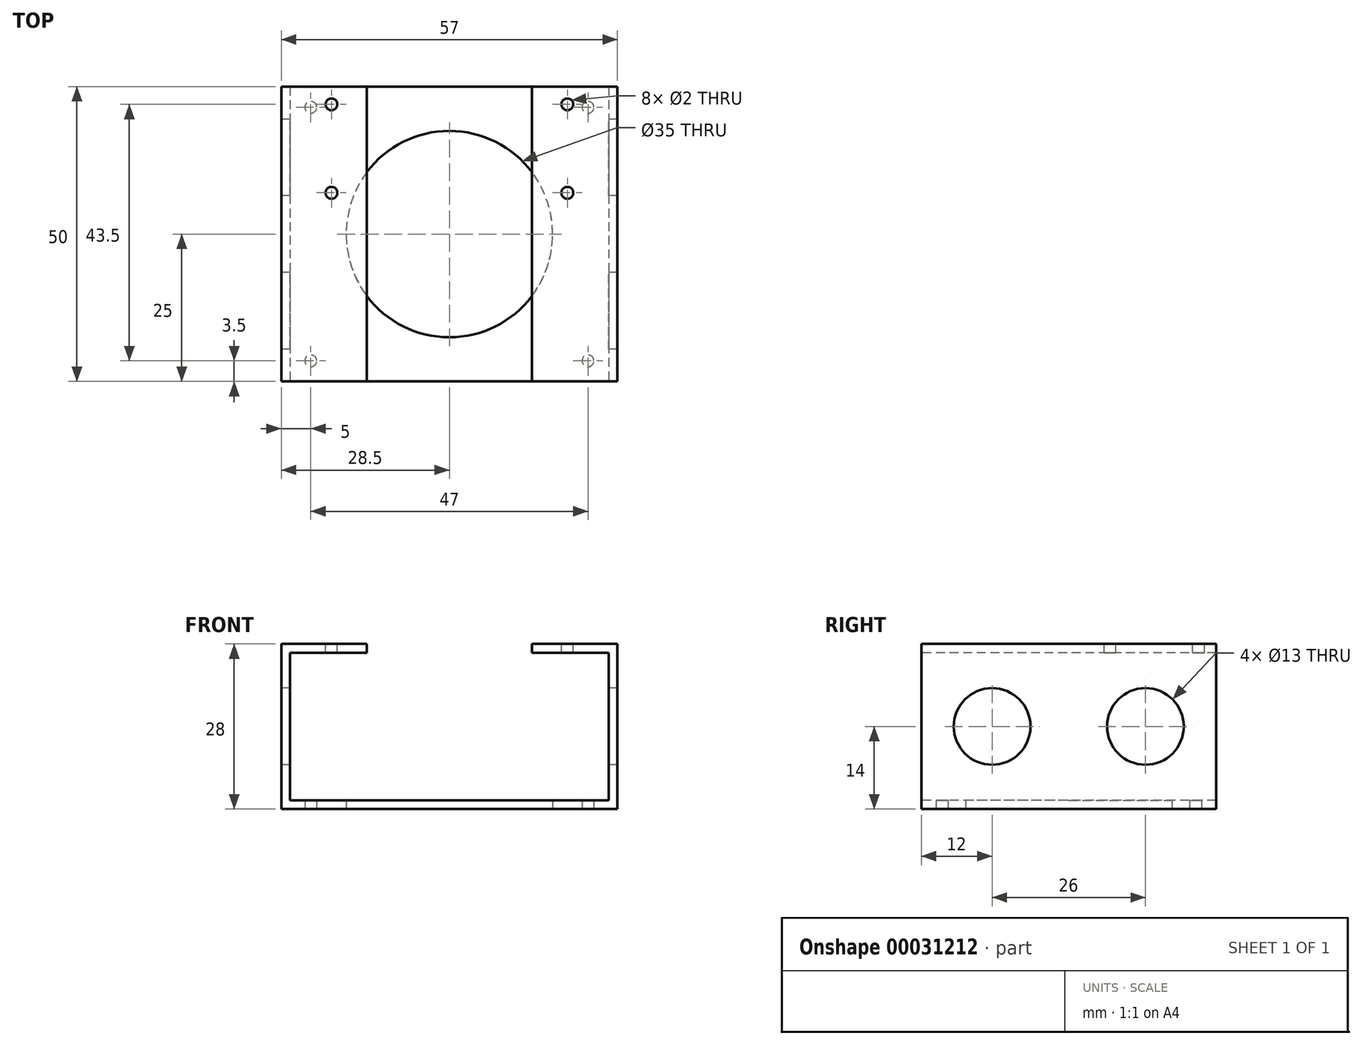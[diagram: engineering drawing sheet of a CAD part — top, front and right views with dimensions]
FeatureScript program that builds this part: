
annotation { "Feature Type Name" : "Feature", "Feature Type Description" : "" }
export const myFeature = defineFeature(function(context is Context, id is Id, definition is map)
    precondition{}
    {
        {
            var Q0;
            Q0=qCreatedBy(makeId("Top.planeOp"),FACE);
            var sketch = newSketch(context, id + "F0", { "sketchPlane" : qUnion([Q0])});
            skLineSegment(sketch, "E0.bottom", {"start": v(-27, 25) * mm, "end": v(27, 25) * mm});
            skLineSegment(sketch, "E0.top", {"start": v(-27, -25) * mm, "end": v(27, -25) * mm});
            skLineSegment(sketch, "E0.left", {"start": v(-27, 25) * mm, "end": v(-27, -25) * mm});
            skLineSegment(sketch, "E0.right", {"start": v(27, 25) * mm, "end": v(27, -25) * mm});
            skPoint(sketch, "E0.middle", {"position": v(0, 0) * mm});
            skLineSegment(sketch, "E1.bottom", {"start": v(-23.5, 21.5) * mm, "end": v(23.5, 21.5) * mm, "construction": true});
            skLineSegment(sketch, "E1.top", {"start": v(-23.5, -21.5) * mm, "end": v(23.5, -21.5) * mm, "construction": true});
            skLineSegment(sketch, "E1.left", {"start": v(-23.5, 21.5) * mm, "end": v(-23.5, -21.5) * mm, "construction": true});
            skLineSegment(sketch, "E1.right", {"start": v(23.5, 21.5) * mm, "end": v(23.5, -21.5) * mm, "construction": true});
            skCircle(sketch, "E2", {"center": v(-23.5, 21.5) * mm, "radius": 1 * mm});
            skCircle(sketch, "E3.MirrorC", {"center": v(23.5, 21.5) * mm, "radius": 1 * mm});
            skCircle(sketch, "E4.MirrorC", {"center": v(-23.5, -21.5) * mm, "radius": 1 * mm});
            skCircle(sketch, "E5.MirrorC", {"center": v(23.5, -21.5) * mm, "radius": 1 * mm});
            skSolve(sketch);
        }
        {
            var Q0;
            Q0 = qSketchRegion(id + "F0", true);
            extrude(context, id + "F1", {"entities" : qUnion([Q0]), "depth" : 1.5 * mm});
        }
        {
            var Q0;
            Q0=qCreatedBy(makeId("Top.planeOp"),FACE);
            var sketch = newSketch(context, id + "F2", { "sketchPlane" : qUnion([Q0])});
            skLineSegment(sketch, "E6.0", {"start": v(27, 25) * mm, "end": v(27, -25) * mm, "construction": true});
            skLineSegment(sketch, "E7.bottom", {"start": v(27, 25) * mm, "end": v(28.5, 25) * mm});
            skLineSegment(sketch, "E7.top", {"start": v(27, -25) * mm, "end": v(28.5, -25) * mm});
            skLineSegment(sketch, "E7.left", {"start": v(27, 25) * mm, "end": v(27, -25) * mm});
            skLineSegment(sketch, "E7.right", {"start": v(28.5, 25) * mm, "end": v(28.5, -25) * mm});
            skSolve(sketch);
        }
        {
            var Q0;
            Q0 = qSketchRegion(id + "F2", true);
            extrude(context, id + "F3", {"entities" : qUnion([Q0]), "operationType" : NewBodyOperationType.ADD, "depth" : (25 + 1.5 + 1.5) * mm});
        }
        {
            var Q0;
            Q0=makeQuery(id+"F3.opExtrude","SWEPT_FACE",FACE,{"disambiguationData":[OSD([sQuery(id+"F2.wireOp",EDGE,"E7.left")])]});
            var sketch = newSketch(context, id + "F4", { "sketchPlane" : qUnion([Q0])});
            skLineSegment(sketch, "E8.bottom", {"start": v(-25, 28) * mm, "end": v(25, 28) * mm});
            skLineSegment(sketch, "E8.top", {"start": v(-25, 26.5) * mm, "end": v(25, 26.5) * mm});
            skLineSegment(sketch, "E8.left", {"start": v(-25, 28) * mm, "end": v(-25, 26.5) * mm});
            skLineSegment(sketch, "E8.right", {"start": v(25, 28) * mm, "end": v(25, 26.5) * mm});
            skSolve(sketch);
        }
        {
            var Q0;
            Q0 = qSketchRegion(id + "F4", true);
            extrude(context, id + "F5", {"entities" : qUnion([Q0]), "operationType" : NewBodyOperationType.ADD, "depth" : 13 * mm});
        }
        {
            var Q0;
            Q0=makeQuery(id+"F5.boolean.opBoolean","MERGE",FACE,{"derivedFrom":[makeQuery(id+"F3.opExtrude","CAP_FACE",FACE,{"disambiguationData":[OSD([sQuery(id+"F2.wireOp",EDGE,"E7.bottom"),sQuery(id+"F2.wireOp",EDGE,"E7.top"),sQuery(id+"F2.wireOp",EDGE,"E7.left"),sQuery(id+"F2.wireOp",EDGE,"E7.right")])],"isStart":false}),makeQuery(id+"F5.opExtrude","SWEPT_FACE",FACE,{"disambiguationData":[OSD([sQuery(id+"F4.wireOp",EDGE,"E8.bottom")])]})]});
            var sketch = newSketch(context, id + "F6", { "sketchPlane" : qUnion([Q0])});
            skCircle(sketch, "E9", {"center": v(20, 22) * mm, "radius": 1 * mm});
            skCircle(sketch, "E10", {"center": v(20, 7) * mm, "radius": 1 * mm});
            skSolve(sketch);
        }
        {
            var Q0;
            Q0 = qSketchRegion(id + "F6", true);
            extrude(context, id + "F7", {"entities" : qUnion([Q0]), "operationType" : NewBodyOperationType.REMOVE, "endBound" : BoundingType.UP_TO_NEXT, "oppositeDirection" : true, "depth" : 25 * mm});
        }
        {
            var Q0;
            Q0=makeQuery(id+"F1.opExtrude","SWEPT_BODY",BODY,{"disambiguationData":[OSD([sQuery(id+"F0.wireOp",EDGE,"E0.bottom"),sQuery(id+"F0.wireOp",EDGE,"E0.top"),sQuery(id+"F0.wireOp",EDGE,"E0.left"),sQuery(id+"F0.wireOp",EDGE,"E0.right"),sQuery(id+"F0.wireOp",EDGE,"E2"),sQuery(id+"F0.wireOp",EDGE,"E3.MirrorC"),sQuery(id+"F0.wireOp",EDGE,"E4.MirrorC"),sQuery(id+"F0.wireOp",EDGE,"E5.MirrorC")])]});
            var Q1;
            Q1=qCreatedBy(makeId("Right.planeOp"),FACE);
            mirror(context, id + "F8", {"operationType" : NewBodyOperationType.ADD, "entities" : qUnion([Q0]), "mirrorPlane" : qUnion([Q1])});
        }
        {
            var Q0;
            Q0=makeQuery(id+"F8.opPattern","COPY",FACE,{"derivedFrom":makeQuery(id+"F3.opExtrude","SWEPT_FACE",FACE,{"disambiguationData":[OSD([sQuery(id+"F2.wireOp",EDGE,"E7.right")])]}),"instanceName":"1"});
            var sketch = newSketch(context, id + "F9", { "sketchPlane" : qUnion([Q0])});
            skLineSegment(sketch, "E11", {"start": v(-25, 14) * mm, "end": v(25, 14) * mm, "construction": true});
            skCircle(sketch, "E12", {"center": v(-13, 14) * mm, "radius": 6.5 * mm});
            skCircle(sketch, "E13.MirrorC", {"center": v(13, 14) * mm, "radius": 6.5 * mm});
            skSolve(sketch);
        }
        {
            var Q0;
            Q0 = qSketchRegion(id + "F9", true);
            extrude(context, id + "F10", {"entities" : qUnion([Q0]), "operationType" : NewBodyOperationType.REMOVE, "endBound" : BoundingType.THROUGH_ALL, "oppositeDirection" : true, "depth" : 25 * mm});
        }
        {
            var Q0;
            {var subQ0=makeQuery(id+"F3.boolean.opBoolean","MERGE",FACE,{"derivedFrom":[makeQuery(id+"F1.opExtrude","CAP_FACE",FACE,{"disambiguationData":[OSD([sQuery(id+"F0.wireOp",EDGE,"E0.bottom"),sQuery(id+"F0.wireOp",EDGE,"E0.top"),sQuery(id+"F0.wireOp",EDGE,"E0.left"),sQuery(id+"F0.wireOp",EDGE,"E0.right"),sQuery(id+"F0.wireOp",EDGE,"E2"),sQuery(id+"F0.wireOp",EDGE,"E3.MirrorC"),sQuery(id+"F0.wireOp",EDGE,"E4.MirrorC"),sQuery(id+"F0.wireOp",EDGE,"E5.MirrorC")])],"isStart":true}),makeQuery(id+"F3.opExtrude","CAP_FACE",FACE,{"disambiguationData":[OSD([sQuery(id+"F2.wireOp",EDGE,"E7.bottom"),sQuery(id+"F2.wireOp",EDGE,"E7.top"),sQuery(id+"F2.wireOp",EDGE,"E7.left"),sQuery(id+"F2.wireOp",EDGE,"E7.right")])],"isStart":true})]});Q0=makeQuery(id+"F8.boolean.opBoolean","MERGE",FACE,{"derivedFrom":[subQ0,makeQuery(id+"F8.opPattern","COPY",FACE,{"derivedFrom":subQ0,"instanceName":"1"})]});}
            var sketch = newSketch(context, id + "F11", { "sketchPlane" : qUnion([Q0])});
            skCircle(sketch, "E14", {"center": v(0, 0) * mm, "radius": 17.5 * mm});
            skSolve(sketch);
        }
        {
            var Q0;
            Q0 = qSketchRegion(id + "F11", true);
            extrude(context, id + "F12", {"entities" : qUnion([Q0]), "operationType" : NewBodyOperationType.REMOVE, "endBound" : BoundingType.UP_TO_NEXT, "oppositeDirection" : true, "depth" : 25 * mm});
        }
    });
